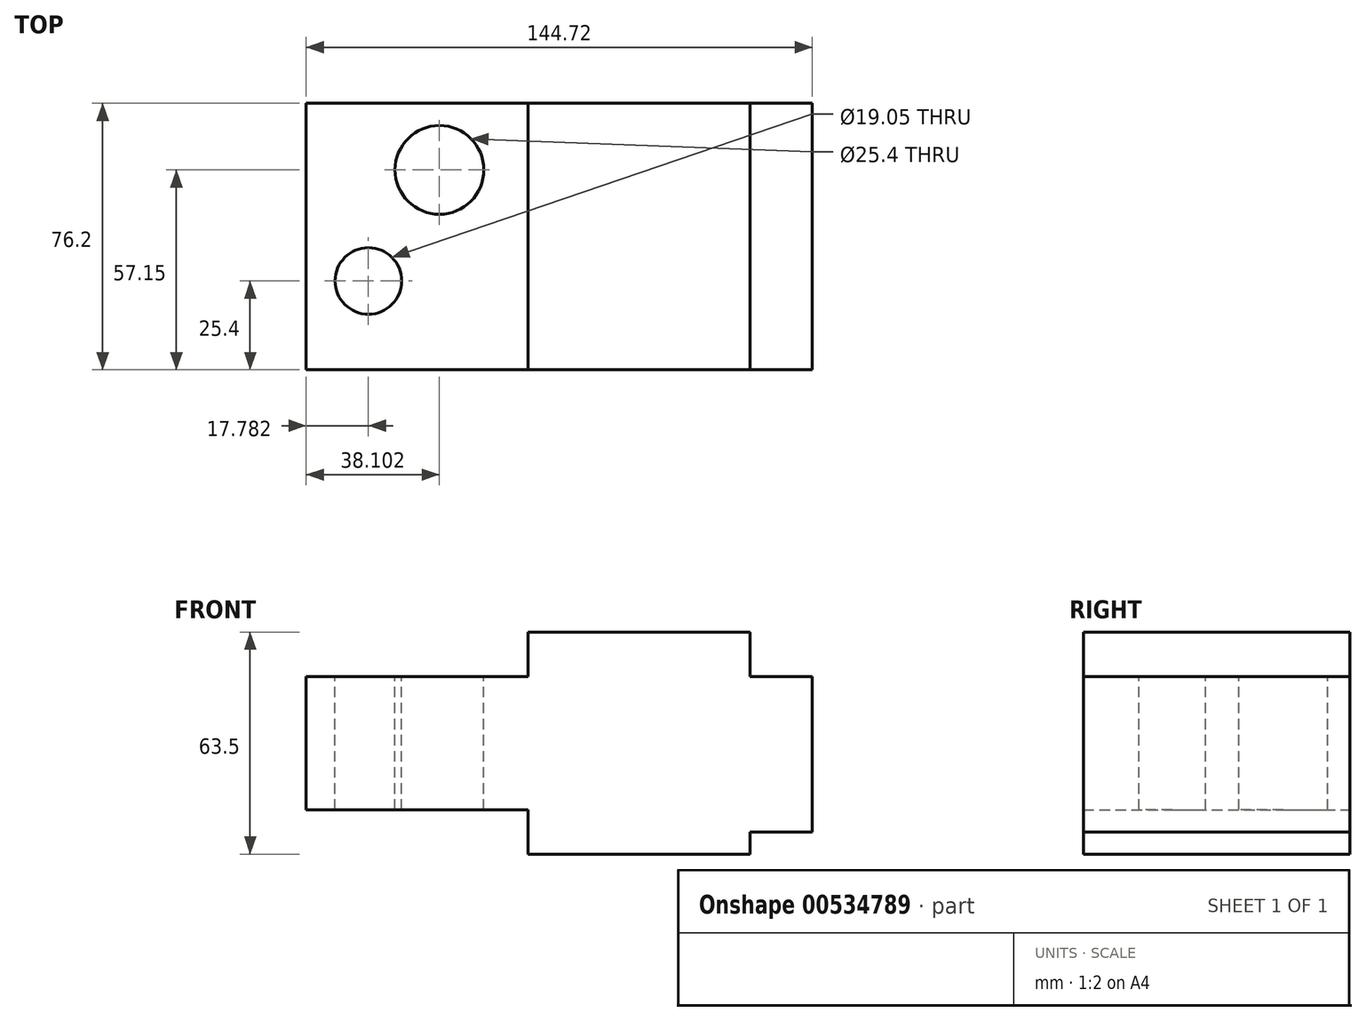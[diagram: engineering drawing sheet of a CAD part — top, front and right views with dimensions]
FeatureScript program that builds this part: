
annotation { "Feature Type Name" : "Feature", "Feature Type Description" : "" }
export const myFeature = defineFeature(function(context is Context, id is Id, definition is map)
    precondition{}
    {
        {
            var Q0;
            Q0=qCreatedBy(makeId("Front.planeOp"),FACE);
            var sketch = newSketch(context, id + "F0", { "sketchPlane" : qUnion([Q0])});
            skLineSegment(sketch, "E0.bottom", {"start": v(-47.6, 44.15) * mm, "end": v(15.9, 44.15) * mm});
            skLineSegment(sketch, "E0.top", {"start": v(-47.6, -19.35) * mm, "end": v(15.9, -19.35) * mm});
            skLineSegment(sketch, "E0.left", {"start": v(-47.6, 44.15) * mm, "end": v(-47.6, 31.45) * mm});
            skLineSegment(sketch, "E0.right", {"start": v(15.9, 44.15) * mm, "end": v(15.9, 31.45) * mm});
            skLineSegment(sketch, "E1.bottom", {"start": v(15.9, 31.45) * mm, "end": v(33.62, 31.45) * mm});
            skLineSegment(sketch, "E1.top", {"start": v(15.9, -13) * mm, "end": v(33.62, -13) * mm});
            skLineSegment(sketch, "E1.right", {"start": v(33.62, 31.45) * mm, "end": v(33.62, -13) * mm});
            skLineSegment(sketch, "E2", {"start": v(-47.6, -6.65) * mm, "end": v(-111.1, -6.65) * mm});
            skLineSegment(sketch, "E3", {"start": v(-111.1, -6.65) * mm, "end": v(-111.1, 31.45) * mm});
            skLineSegment(sketch, "E4", {"start": v(-111.1, 31.45) * mm, "end": v(-47.6, 31.45) * mm});
            skLineSegment(sketch, "E5.trimOffspring", {"start": v(-47.6, -6.65) * mm, "end": v(-47.6, -19.35) * mm});
            skLineSegment(sketch, "E6.trimOffspring", {"start": v(15.9, -13) * mm, "end": v(15.9, -19.35) * mm});
            skSolve(sketch);
        }
        {
            var Q0;
            Q0 = qSketchRegion(id + "F0", true);
            extrude(context, id + "F1", {"entities" : qUnion([Q0]), "depth" : 76.2 * mm, "offsetDistance" : 25.4 * mm});
        }
        {
            var Q0;
            Q0=makeQuery(id+"F1.opExtrude","SWEPT_FACE",FACE,{"disambiguationData":[OSD([sQuery(id+"F0.wireOp",EDGE,"E4")])]});
            var sketch = newSketch(context, id + "F2", { "sketchPlane" : qUnion([Q0])});
            skCircle(sketch, "E7", {"center": v(-73, -19.05) * mm, "radius": 12.7 * mm});
            skCircle(sketch, "E8", {"center": v(-93.32, -50.8) * mm, "radius": 9.53 * mm});
            skSolve(sketch);
        }
        {
            var Q0;
            Q0 = qSketchRegion(id + "F2", true);
            extrude(context, id + "F3", {"entities" : qUnion([Q0]), "operationType" : NewBodyOperationType.REMOVE, "endBound" : BoundingType.UP_TO_NEXT, "oppositeDirection" : true, "depth" : 38.1 * mm, "offsetDistance" : 25.4 * mm});
        }
    });
